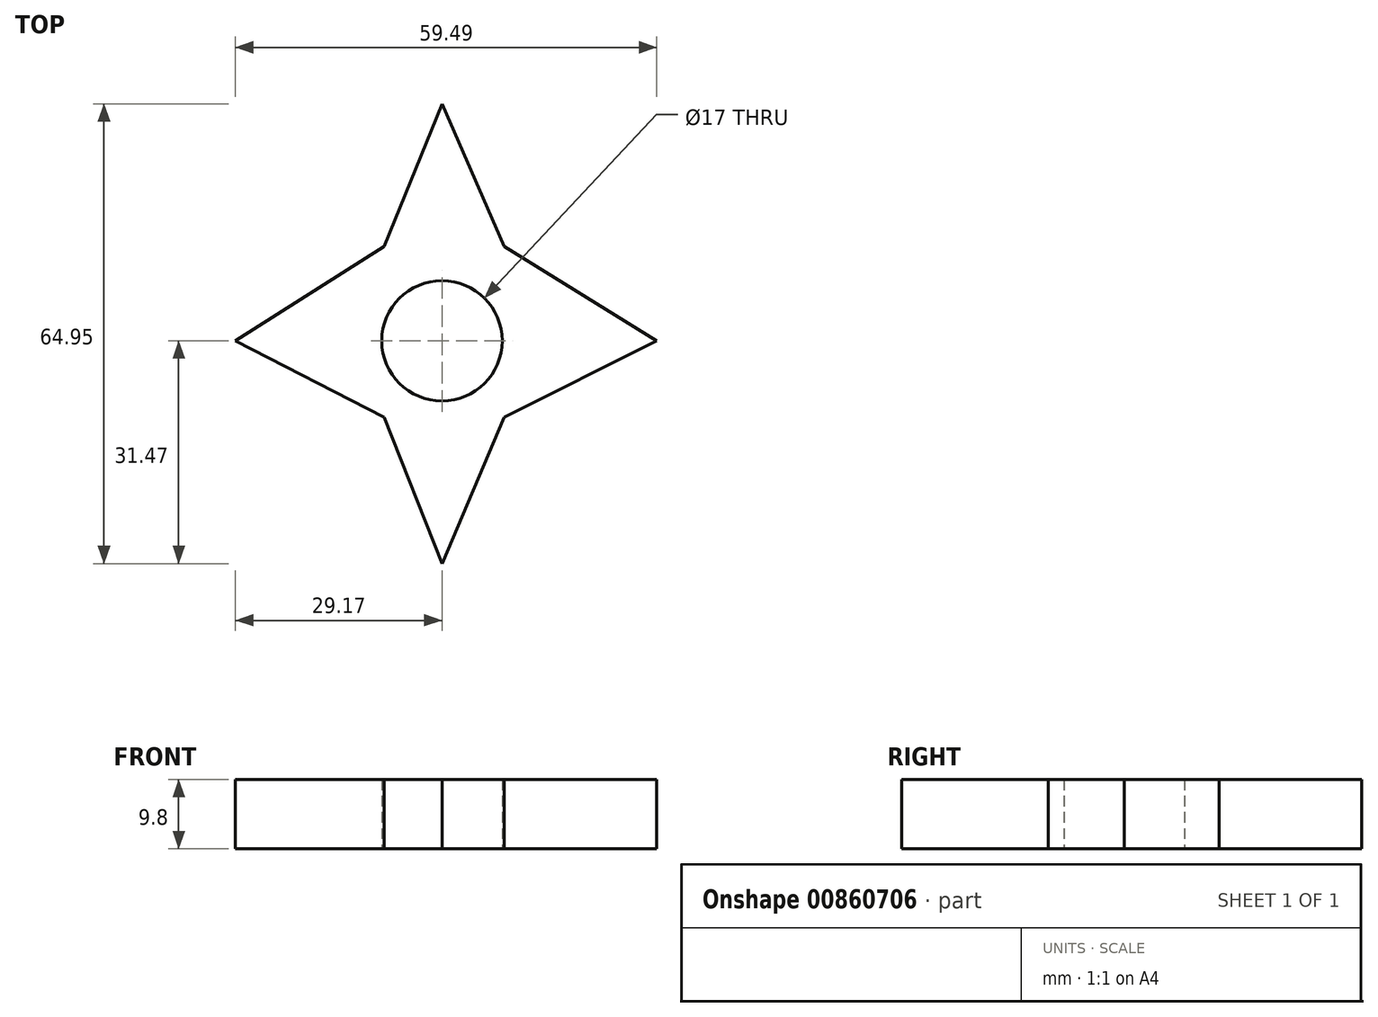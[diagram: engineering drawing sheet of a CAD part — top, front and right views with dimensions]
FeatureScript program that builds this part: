
annotation { "Feature Type Name" : "Feature", "Feature Type Description" : "" }
export const myFeature = defineFeature(function(context is Context, id is Id, definition is map)
    precondition{}
    {
        {
            var Q0;
            Q0=qCreatedBy(makeId("Top.planeOp"),FACE);
            var sketch = newSketch(context, id + "F0", { "sketchPlane" : qUnion([Q0])});
            skCircle(sketch, "E0", {"center": v(0, 0) * mm, "radius": 8.5 * mm});
            skLineSegment(sketch, "E1", {"start": v(8.77, 13.36) * mm, "end": v(30.32, 0) * mm});
            skLineSegment(sketch, "E2", {"start": v(30.32, 0) * mm, "end": v(8.77, -10.78) * mm});
            skLineSegment(sketch, "E3", {"start": v(-8.2, -10.78) * mm, "end": v(-29.17, 0) * mm});
            skLineSegment(sketch, "E4", {"start": v(-8.2, 13.36) * mm, "end": v(-29.17, 0) * mm});
            skLineSegment(sketch, "E5", {"start": v(-8.2, -10.78) * mm, "end": v(0, -31.47) * mm});
            skLineSegment(sketch, "E6", {"start": v(8.77, -10.78) * mm, "end": v(0, -31.47) * mm});
            skLineSegment(sketch, "E7", {"start": v(-8.2, 13.36) * mm, "end": v(0, 33.48) * mm});
            skLineSegment(sketch, "E8", {"start": v(0, 33.48) * mm, "end": v(8.77, 13.36) * mm});
            skSolve(sketch);
        }
        {
            var Q0;
            Q0 = qSketchRegion(id + "F0", true);
            extrude(context, id + "F1", {"entities" : qUnion([Q0]), "depth" : 9.8 * mm, "offsetDistance" : 25 * mm});
        }
    });
